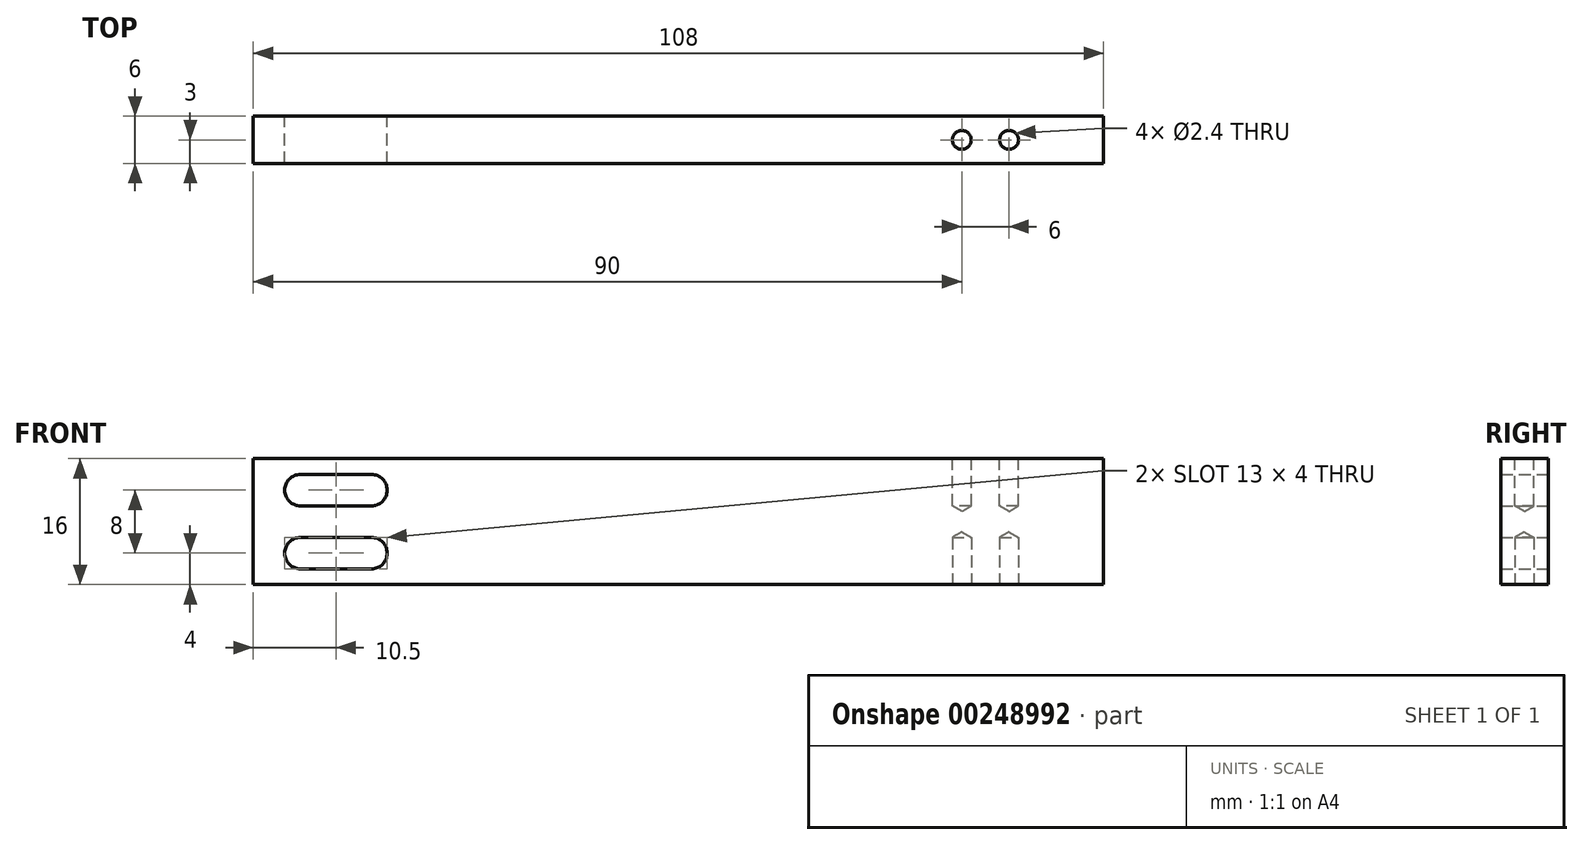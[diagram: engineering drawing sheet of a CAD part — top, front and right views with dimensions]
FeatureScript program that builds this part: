
annotation { "Feature Type Name" : "Feature", "Feature Type Description" : "" }
export const myFeature = defineFeature(function(context is Context, id is Id, definition is map)
    precondition{}
    {
        {
            var Q0;
            Q0=qCreatedBy(makeId("Front.planeOp"),FACE);
            var sketch = newSketch(context, id + "F0", { "sketchPlane" : qUnion([Q0])});
            skLineSegment(sketch, "E0.bottom", {"start": v(54, 8) * mm, "end": v(-54, 8) * mm});
            skLineSegment(sketch, "E0.top", {"start": v(54, -8) * mm, "end": v(-54, -8) * mm});
            skLineSegment(sketch, "E0.left", {"start": v(54, 8) * mm, "end": v(54, -8) * mm});
            skLineSegment(sketch, "E0.right", {"start": v(-54, 8) * mm, "end": v(-54, -8) * mm});
            skPoint(sketch, "E0.middle", {"position": v(0, 0) * mm});
            skLineSegment(sketch, "E1.bottom", {"start": v(-39, 2) * mm, "end": v(-48, 2) * mm});
            skLineSegment(sketch, "E1.top", {"start": v(-39, 6) * mm, "end": v(-48, 6) * mm});
            skLineSegment(sketch, "E1.left", {"start": v(-39, 2) * mm, "end": v(-39, 6) * mm});
            skLineSegment(sketch, "E1.right", {"start": v(-48, 2) * mm, "end": v(-48, 6) * mm});
            skPoint(sketch, "E1.middle", {"position": v(-43.5, 4) * mm});
            skLineSegment(sketch, "E2.bottom", {"start": v(-39, -6) * mm, "end": v(-48, -6) * mm});
            skLineSegment(sketch, "E2.top", {"start": v(-39, -2) * mm, "end": v(-48, -2) * mm});
            skLineSegment(sketch, "E2.left", {"start": v(-39, -6) * mm, "end": v(-39, -2) * mm});
            skLineSegment(sketch, "E2.right", {"start": v(-48, -6) * mm, "end": v(-48, -2) * mm});
            skPoint(sketch, "E2.middle", {"position": v(-43.5, -4) * mm});
            skArc(sketch, "E3", {"start": v(-39, 6) * mm, "mid": v(-37, 4) * mm, "end": v(-39, 2) * mm});
            skArc(sketch, "E4", {"start": v(-48, 6) * mm, "mid": v(-50, 4) * mm, "end": v(-48, 2) * mm});
            skArc(sketch, "E5", {"start": v(-39, -2) * mm, "mid": v(-37, -4) * mm, "end": v(-39, -6) * mm});
            skArc(sketch, "E6", {"start": v(-48, -6) * mm, "mid": v(-50, -4) * mm, "end": v(-48, -2) * mm});
            skSolve(sketch);
        }
        {
            var Q0;
            Q0=makeQuery(id+"F0.imprint","IMPRINT",FACE,{"disambiguationData":[TD([[makeQuery(id+"F0.imprint","IMPRINT",EDGE,{"derivedFrom":sQuery(id+"F0.wireOp",EDGE,"E0.bottom")}),1.0]])]});
            extrude(context, id + "F1", {"entities" : qUnion([Q0]), "endBound" : BoundingType.SYMMETRIC, "depth" : 6 * mm});
        }
        {
            var Q0;
            Q0=makeQuery(id+"F1.opExtrude","SWEPT_FACE",FACE,{"disambiguationData":[OSD([sQuery(id+"F0.wireOp",EDGE,"E0.top")])]});
            var sketch = newSketch(context, id + "F2", { "sketchPlane" : qUnion([Q0])});
            skPoint(sketch, "E7", {"position": v(42, 0) * mm});
            skPoint(sketch, "E8", {"position": v(36, 0) * mm});
            skPoint(sketch, "E9", {"position": v(54, 0) * mm});
            skSolve(sketch);
        }
        {
            var Q0;
            Q0=sQuery(id+"F2.wireOp",VERTEX,"E8");
            var Q1;
            Q1=sQuery(id+"F2.wireOp",VERTEX,"E7");
            var Q2;
            Q2=makeQuery(id+"F1.opExtrude","SWEPT_BODY",BODY,{"disambiguationData":[OSD([sQuery(id+"F0.wireOp",EDGE,"E0.bottom"),sQuery(id+"F0.wireOp",EDGE,"E0.top"),sQuery(id+"F0.wireOp",EDGE,"E0.left"),sQuery(id+"F0.wireOp",EDGE,"E0.right"),sQuery(id+"F0.wireOp",EDGE,"E1.bottom"),sQuery(id+"F0.wireOp",EDGE,"E1.top"),sQuery(id+"F0.wireOp",EDGE,"E2.bottom"),sQuery(id+"F0.wireOp",EDGE,"E2.top"),sQuery(id+"F0.wireOp",EDGE,"E3"),sQuery(id+"F0.wireOp",EDGE,"E4"),sQuery(id+"F0.wireOp",EDGE,"E5"),sQuery(id+"F0.wireOp",EDGE,"E6")])]});
            hole(context, id + "F3", {"style" : HoleStyle.SIMPLE, "endStyle" : HoleEndStyle.BLIND, "standardTappedOrClearance" : lookupTablePath({ "standard" : "ISO", "engagement" : "75%", "pitch" : "0.6 mm", "size" : "M3", "type" : "Tapped" }), "standardBlindInLast" : lookupTablePath({ "standard" : "ISO", "engagement" : "75%", "pitch" : "0.6 mm", "size" : "M3", "type" : "Tapped" }), "holeDiameter" : 2.4 * mm, "showTappedDepth" : true, "holeDepth" : 6 * mm, "tappedDepth" : 4.2 * mm, "tapClearance" : 3, "startFromSketch" : true, "locations" : qUnion([Q0, Q1]), "scope" : qUnion([Q2])});
        }
        {
            var Q0;
            Q0=makeQuery(id+"F1.opExtrude","SWEPT_FACE",FACE,{"disambiguationData":[OSD([sQuery(id+"F0.wireOp",EDGE,"E0.bottom")])]});
            var sketch = newSketch(context, id + "F4", { "sketchPlane" : qUnion([Q0])});
            skPoint(sketch, "E10.0", {"position": v(36, 0) * mm});
            skPoint(sketch, "E11.0", {"position": v(42, 0) * mm});
            skSolve(sketch);
        }
        {
            var Q0;
            Q0=sQuery(id+"F4.wireOp",VERTEX,"E10.0");
            var Q1;
            Q1=sQuery(id+"F4.wireOp",VERTEX,"E11.0");
            var Q2;
            Q2=makeQuery(id+"F1.opExtrude","SWEPT_BODY",BODY,{"disambiguationData":[OSD([sQuery(id+"F0.wireOp",EDGE,"E0.bottom"),sQuery(id+"F0.wireOp",EDGE,"E0.top"),sQuery(id+"F0.wireOp",EDGE,"E0.left"),sQuery(id+"F0.wireOp",EDGE,"E0.right"),sQuery(id+"F0.wireOp",EDGE,"E1.bottom"),sQuery(id+"F0.wireOp",EDGE,"E1.top"),sQuery(id+"F0.wireOp",EDGE,"E2.bottom"),sQuery(id+"F0.wireOp",EDGE,"E2.top"),sQuery(id+"F0.wireOp",EDGE,"E3"),sQuery(id+"F0.wireOp",EDGE,"E4"),sQuery(id+"F0.wireOp",EDGE,"E5"),sQuery(id+"F0.wireOp",EDGE,"E6")])]});
            hole(context, id + "F5", {"style" : HoleStyle.SIMPLE, "endStyle" : HoleEndStyle.BLIND, "standardTappedOrClearance" : lookupTablePath({ "standard" : "ISO", "engagement" : "75%", "pitch" : "0.6 mm", "size" : "M3", "type" : "Tapped" }), "standardBlindInLast" : lookupTablePath({ "standard" : "ISO", "engagement" : "75%", "pitch" : "0.6 mm", "size" : "M3", "type" : "Tapped" }), "holeDiameter" : 2.4 * mm, "showTappedDepth" : true, "holeDepth" : 6 * mm, "tappedDepth" : 4.2 * mm, "tapClearance" : 3, "startFromSketch" : true, "locations" : qUnion([Q0, Q1]), "scope" : qUnion([Q2])});
        }
    });
